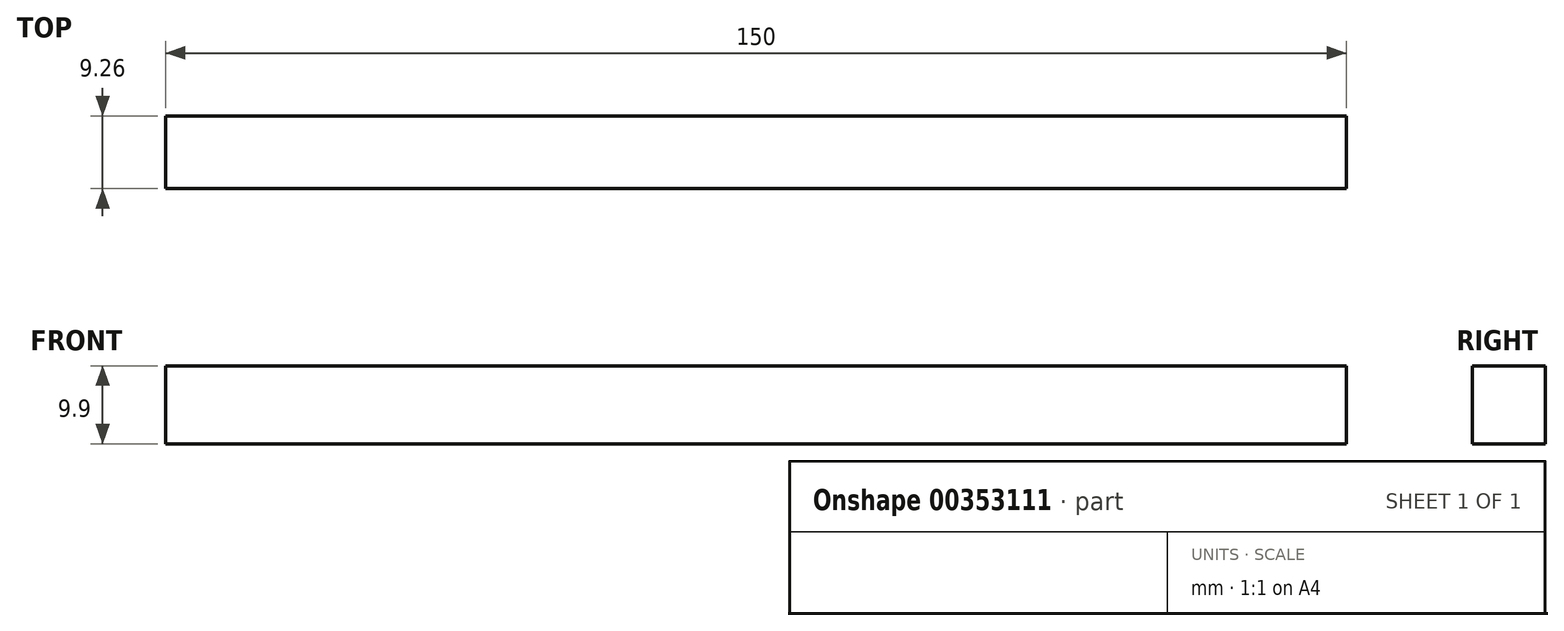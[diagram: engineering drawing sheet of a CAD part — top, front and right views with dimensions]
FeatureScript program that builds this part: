
annotation { "Feature Type Name" : "Feature", "Feature Type Description" : "" }
export const myFeature = defineFeature(function(context is Context, id is Id, definition is map)
    precondition{}
    {
        {
            var Q0;
            Q0=qCreatedBy(makeId("Top.planeOp"),FACE);
            var sketch = newSketch(context, id + "F0", { "sketchPlane" : qUnion([Q0])});
            skLineSegment(sketch, "E0.bottom", {"start": v(0, 0) * mm, "end": v(150, 0) * mm});
            skLineSegment(sketch, "E0.top", {"start": v(0, 9.26) * mm, "end": v(150, 9.26) * mm});
            skLineSegment(sketch, "E0.left", {"start": v(0, 0) * mm, "end": v(0, 9.26) * mm});
            skLineSegment(sketch, "E0.right", {"start": v(150, 0) * mm, "end": v(150, 9.26) * mm});
            skSolve(sketch);
        }
        {
            var Q0;
            Q0=makeQuery(id+"F0.imprint","IMPRINT",FACE,{"disambiguationData":[TD([[makeQuery(id+"F0.imprint","IMPRINT",EDGE,{"derivedFrom":sQuery(id+"F0.wireOp",EDGE,"E0.bottom")}),1.0]])]});
            extrude(context, id + "F1", {"entities" : qUnion([Q0]), "depth" : 9.9 * mm});
        }
    });
